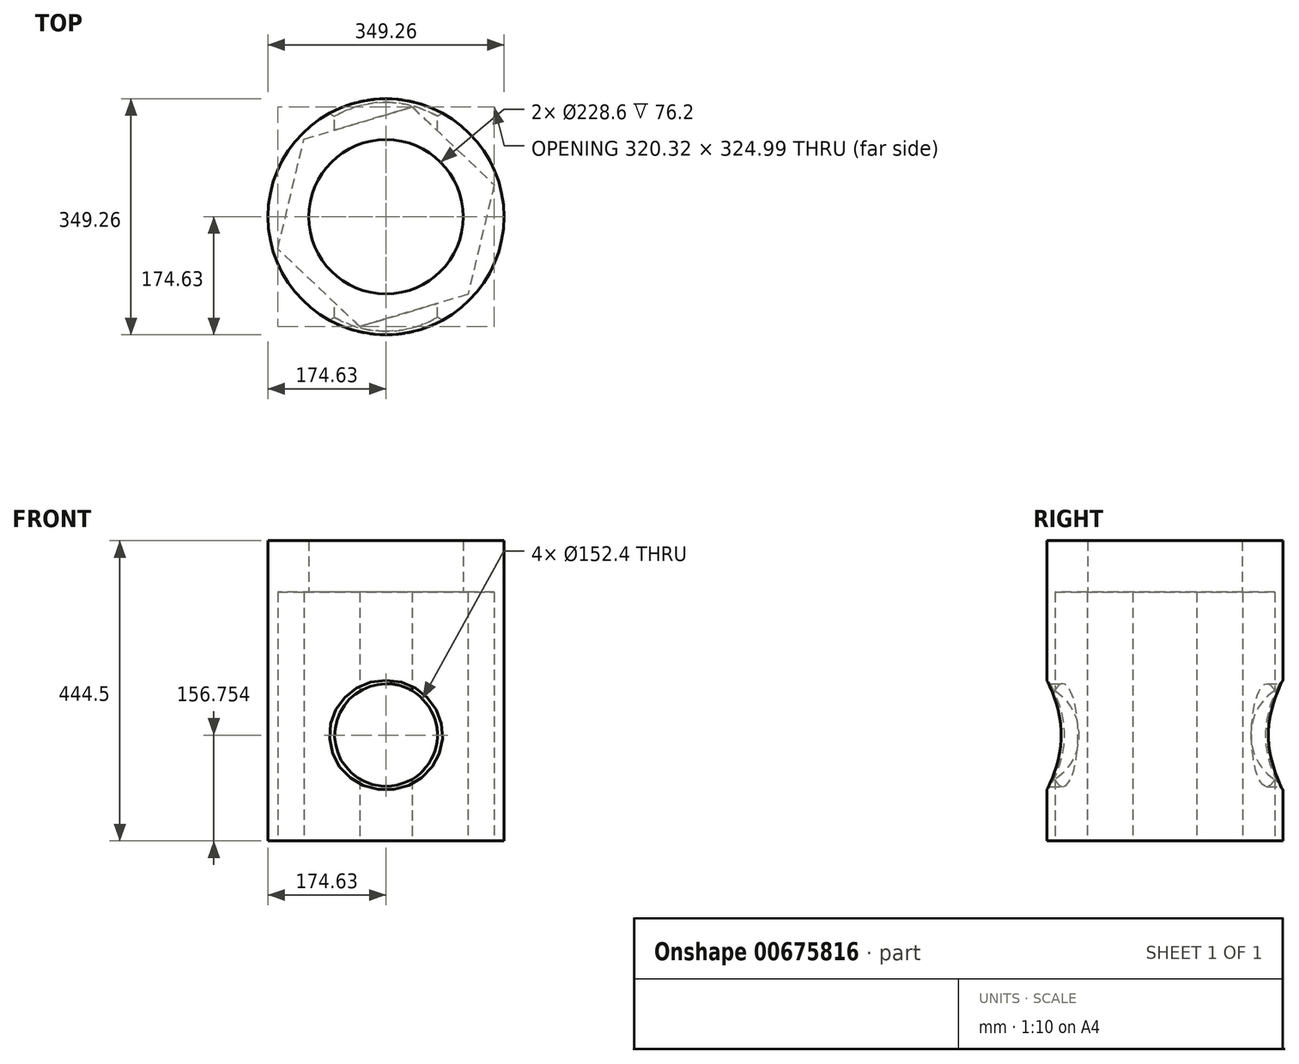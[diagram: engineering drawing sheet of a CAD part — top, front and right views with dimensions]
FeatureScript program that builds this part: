
annotation { "Feature Type Name" : "Feature", "Feature Type Description" : "" }
export const myFeature = defineFeature(function(context is Context, id is Id, definition is map)
    precondition{}
    {
        {
            var Q0;
            Q0=qCreatedBy(makeId("Top.planeOp"),FACE);
            var sketch = newSketch(context, id + "F0", { "sketchPlane" : qUnion([Q0])});
            skCircle(sketch, "E0", {"center": v(0, 0) * mm, "radius": 174.63 * mm});
            skSolve(sketch);
        }
        {
            var Q0;
            Q0 = qSketchRegion(id + "F0", true);
            extrude(context, id + "F1", {"entities" : qUnion([Q0]), "depth" : 444.5 * mm, "offsetDistance" : 25.4 * mm});
        }
        {
            var Q0;
            Q0=qCreatedBy(makeId("Top.planeOp"),FACE);
            var sketch = newSketch(context, id + "F2", { "sketchPlane" : qUnion([Q0])});
            skCircle(sketch, "E1.cCircle", {"center": v(0, 0) * mm, "radius": 167.08 * mm, "construction": true});
            skLineSegment(sketch, "E1.0", {"start": v(38.87, 162.5) * mm, "end": v(160.16, 47.59) * mm});
            skLineSegment(sketch, "E1.1", {"start": v(160.16, 47.59) * mm, "end": v(121.3, -114.9) * mm});
            skLineSegment(sketch, "E1.2", {"start": v(121.3, -114.9) * mm, "end": v(-38.87, -162.5) * mm});
            skLineSegment(sketch, "E1.3", {"start": v(-38.87, -162.5) * mm, "end": v(-160.16, -47.59) * mm});
            skLineSegment(sketch, "E1.4", {"start": v(-160.16, -47.59) * mm, "end": v(-121.3, 114.9) * mm});
            skLineSegment(sketch, "E1.5", {"start": v(-121.3, 114.9) * mm, "end": v(38.87, 162.5) * mm});
            skSolve(sketch);
        }
        {
            var Q0;
            Q0=makeQuery(id+"F2.imprint","IMPRINT",FACE,{"disambiguationData":[TD([[makeQuery(id+"F2.imprint","IMPRINT",EDGE,{"derivedFrom":sQuery(id+"F2.wireOp",EDGE,"E1.0")}),-1.0]])]});
            extrude(context, id + "F3", {"entities" : qUnion([Q0]), "operationType" : NewBodyOperationType.REMOVE, "depth" : 368.3 * mm, "offsetDistance" : 25.4 * mm});
        }
        {
            var Q0;
            Q0=qCreatedBy(makeId("Top.planeOp"),FACE);
            var sketch = newSketch(context, id + "F4", { "sketchPlane" : qUnion([Q0])});
            skCircle(sketch, "E2", {"center": v(0, 0) * mm, "radius": 114.3 * mm});
            skSolve(sketch);
        }
        {
            var Q0;
            Q0=makeQuery(id+"F4.imprint","IMPRINT",FACE,{"disambiguationData":[TD([[makeQuery(id+"F4.imprint","IMPRINT",EDGE,{"derivedFrom":sQuery(id+"F4.wireOp",EDGE,"E2")}),1.0]])]});
            extrude(context, id + "F5", {"entities" : qUnion([Q0]), "operationType" : NewBodyOperationType.REMOVE, "depth" : 579.88 * mm, "offsetDistance" : 25.4 * mm});
        }
        {
            var Q0;
            Q0=qCreatedBy(makeId("Front.planeOp"),FACE);
            var sketch = newSketch(context, id + "F6", { "sketchPlane" : qUnion([Q0])});
            skCircle(sketch, "E3", {"center": v(0, 156.75) * mm, "radius": 76.2 * mm});
            skSolve(sketch);
        }
        {
            var Q0;
            Q0 = qSketchRegion(id + "F6", true);
            extrude(context, id + "F7", {"entities" : qUnion([Q0]), "operationType" : NewBodyOperationType.REMOVE, "endBound" : BoundingType.SYMMETRIC, "depth" : 426.72 * mm, "offsetDistance" : 25.4 * mm});
        }
        {
            var Q0;
            Q0=makeQuery(id+"F7.boolean.opBoolean","INTERSECT",EDGE,{"disambiguationData":[OD(0.0)],"derivedFrom":[makeQuery(id+"F1.opExtrude","SWEPT_FACE",FACE,{"disambiguationData":[OSD([sQuery(id+"F0.wireOp",EDGE,"E0")])]}),makeQuery(id+"F7.opExtrude","SWEPT_FACE",FACE,{"disambiguationData":[OSD([sQuery(id+"F6.wireOp",EDGE,"E3")])]})]});
            chamfer(context, id + "F8", {"entities" : qUnion([Q0]), "width" : 5.08 * mm, "tangentPropagation" : true});
        }
        {
            var Q0;
            Q0=makeQuery(id+"F7.boolean.opBoolean","INTERSECT",EDGE,{"disambiguationData":[OD(1.0)],"derivedFrom":[makeQuery(id+"F1.opExtrude","SWEPT_FACE",FACE,{"disambiguationData":[OSD([sQuery(id+"F0.wireOp",EDGE,"E0")])]}),makeQuery(id+"F7.opExtrude","SWEPT_FACE",FACE,{"disambiguationData":[OSD([sQuery(id+"F6.wireOp",EDGE,"E3")])]})]});
            chamfer(context, id + "F9", {"entities" : qUnion([Q0]), "width" : 5.08 * mm, "tangentPropagation" : true});
        }
    });
